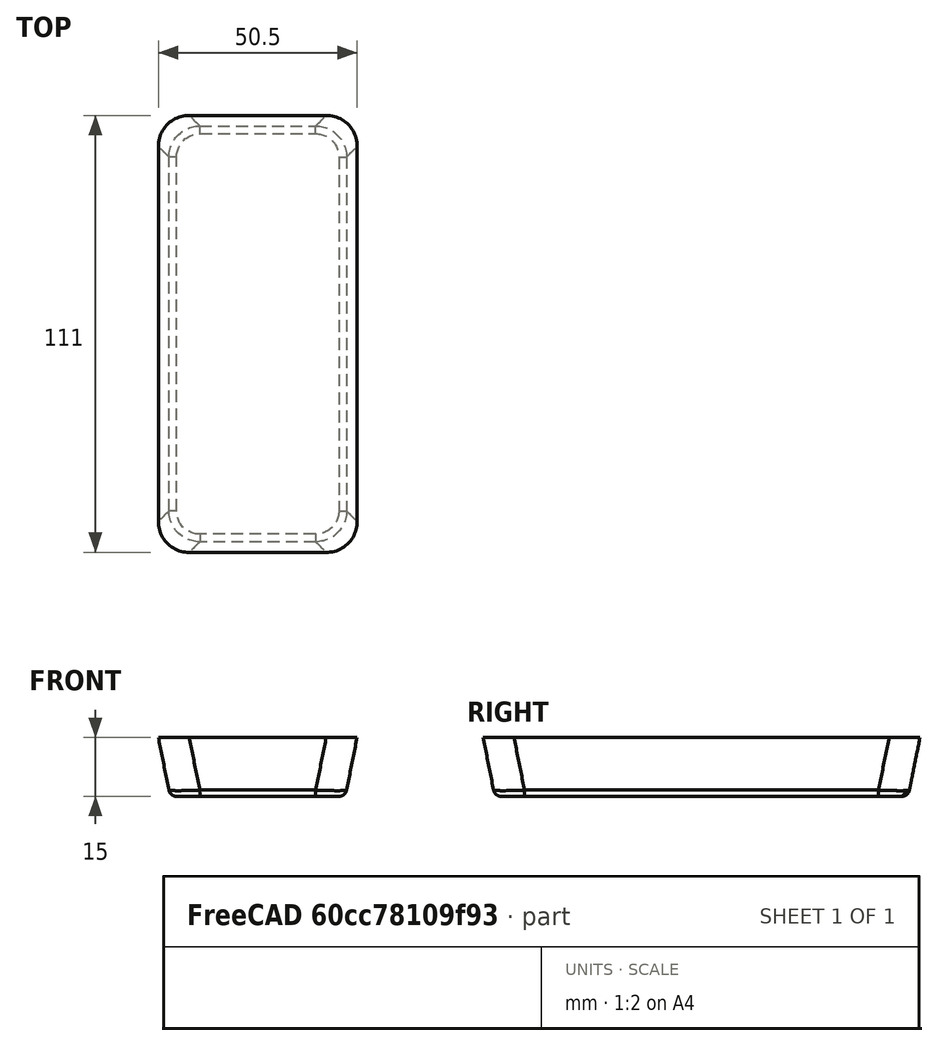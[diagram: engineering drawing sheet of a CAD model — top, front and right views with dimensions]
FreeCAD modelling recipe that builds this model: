
FCSTD DOCUMENT  (FreeCAD 0.20R29603 (Git))
Label: ParametricTray
License: All rights reserved
LicenseURL: http://en.wikipedia.org/wiki/All_rights_reserved
objects: TechDraw::DrawViewDimension×4, Sketcher::SketchObject×2, PartDesign::Fillet×2, TechDraw::DrawProjGroupItem×2, TechDraw::DrawViewBalloon×2, Spreadsheet::Sheet×1, PartDesign::AdditiveLoft×1, PartDesign::Body×1, TechDraw::DrawSVGTemplate×1, TechDraw::DrawProjGroup×1, TechDraw::DrawPage×1
note: 9 computed .brp shape members not serialized (recipe doc carries the construction recipe); baked Part::Feature solids carry a one-line shape summary decoded from their .brp

FEATURE [Spreadsheet::Sheet] Spreadsheet  label="data"
  cells = A1=Height; B1(height)==15mm; A2=Length; B2(length)==111mm; A3=Width; B3(width)==50.5mm; A4=Side Radius; B4(r_s)==8mm; A5=Bottom Radius; B5(r_b)==2mm; A6=Wall Gap; B6(gap)==3mm
FEATURE [Sketcher::SketchObject] Sketch  label="TopSketch"
  AttachmentOffset = pos=(0,0,15) rot=(0,0,1;0rad)
  FullyConstrained = true
  MapMode = 5
  Placement = pos=(0,0,15) rot=(0,0,1;0rad)
  Support = -> [XY_Plane]
  expr: .AttachmentOffset.Base.z = <<data>>.height
  expr: Constraints[10] = <<data>>.width
  expr: Constraints[9] = <<data>>.length
  sketch-geometry (4):
    g0: LineSegment StartX=0 StartY=0 StartZ=0 EndX=50.5 EndY=0 EndZ=0
    g1: LineSegment StartX=50.5 StartY=0 StartZ=0 EndX=50.5 EndY=111 EndZ=0
    g2: LineSegment StartX=50.5 StartY=111 StartZ=0 EndX=0 EndY=111 EndZ=0
    g3: LineSegment StartX=0 StartY=111 StartZ=0 EndX=0 EndY=0 EndZ=0
  constraints (11):
    c: Coincident(g0,g1)
    c: Coincident(g1,g2)
    c: Coincident(g2,g3)
    c: Coincident(g3,g0)
    c: Horizontal(g0)
    c: Horizontal(g2)
    c: Vertical(g1)
    c: Vertical(g3)
    c: Coincident(g0,g-1)
    c: DistanceY(g1,g1) = 111
    c: DistanceX(g0,g0) = 50.5
FEATURE [Sketcher::SketchObject] Sketch001  label="BottomSketch"
  ExternalGeometry = -> [Sketch]
  FullyConstrained = true
  MapMode = 5
  Support = -> [XY_Plane]
  expr: Constraints[10] = <<data>>.gap
  expr: Constraints[11] = <<data>>.gap
  expr: Constraints[8] = <<data>>.gap
  expr: Constraints[9] = <<data>>.gap
  sketch-geometry (4):
    g0: LineSegment StartX=3 StartY=108 StartZ=0 EndX=47.5 EndY=108 EndZ=0
    g1: LineSegment StartX=47.5 StartY=108 StartZ=0 EndX=47.5 EndY=3 EndZ=0
    g2: LineSegment StartX=47.5 StartY=3 StartZ=0 EndX=3 EndY=3 EndZ=0
    g3: LineSegment StartX=3 StartY=3 StartZ=0 EndX=3 EndY=108 EndZ=0
  constraints (12):
    c: Coincident(g0,g1)
    c: Coincident(g1,g2)
    c: Coincident(g2,g3)
    c: Coincident(g3,g0)
    c: Horizontal(g0)
    c: Horizontal(g2)
    c: Vertical(g1)
    c: Vertical(g3)
    c: DistanceX(g-3,g0) = 3
    c: DistanceY(g0,g-3) = 3
    c: DistanceY(g-4,g1) = 3
    c: DistanceX(g1,g-4) = 3
FEATURE [PartDesign::AdditiveLoft] AdditiveLoft
  Closed = false
  Profile = -> Sketch001
  Ruled = false
  Sections = -> [Sketch]
FEATURE [PartDesign::Fillet] Fillet
  Base = -> AdditiveLoft [Edge12,Edge11,Edge5,Edge7]
  BaseFeature = -> AdditiveLoft
  Radius = 8
  SupportTransform = false
  UseAllEdges = false
  expr: Radius = <<data>>.r_s
FEATURE [PartDesign::Fillet] Fillet001
  Base = -> Fillet [Face1]
  BaseFeature = -> Fillet
  Radius = 2
  SupportTransform = false
  UseAllEdges = false
  expr: Radius = <<data>>.r_b
FEATURE [PartDesign::Body] Body
  Group = -> [Sketch,Sketch001,AdditiveLoft,Fillet,Fillet001]
  Origin = -> Origin
  Tip = -> Fillet001
FEATURE [TechDraw::DrawSVGTemplate] Template
  EditableTexts = AUTHOR_NAME=<owner>; DN=DN; DRAWING_TITLE=Parametric Tray; FC-DATE=05/03/2023; FC-REV=REV A; FC-SC=SCALE; FC-SH=1 / 1; FC-SI=A4; FreeCAD_DRAWING=Parameters; PN=PN
  Height = 297
  Orientation = 0
  Width = 210
FEATURE [TechDraw::DrawProjGroupItem] ProjItem  label="Front"
  CoarseView = false
  Direction = (1,1e-16,0)
  Focus = 100
  HardHidden = false
  IsoCount = 0
  IsoHidden = false
  IsoVisible = false
  LockPosition = true
  Perspective = false
  Rotation = 0
  RotationVector = (-1,0,0)
  ScaleType = 2
  SeamHidden = false
  SeamVisible = true
  SmoothHidden = false
  SmoothVisible = true
  Source = -> [Body]
  Type = 0
  X = 0
  XDirection = (-1e-16,1,0)
  Y = 0
FEATURE [TechDraw::DrawViewBalloon] Balloon
  BubbleShape = 1
  EndType = 0
  EndTypeScale = 1
  KinkLength = 5
  LockPosition = false
  OriginX = 52.7607
  OriginY = -7.12815
  Rotation = 0
  ScaleType = 0
  ShapeScale = 1
  SourceView = -> ProjItem
  Text = Bottom Radius
  TextWrapLen = -1
  X = 41.1133
  Y = -20.7332
FEATURE [TechDraw::DrawViewDimension] Dimension002
  AngleOverride = false
  Arbitrary = true
  ArbitraryTolerances = false
  EqualTolerance = true
  ExtensionAngle = 0
  FormatSpec = Height
  FormatSpecOverTolerance = %+.2w
  FormatSpecUnderTolerance = %+.2w
  Inverted = false
  LineAngle = 0
  LockPosition = false
  MeasureType = 1
  OverTolerance = 0
  References2D = -> [ProjItem]
  Rotation = 0
  ScaleType = 0
  TheoreticalExact = false
  Type = 2
  UnderTolerance = 0
  X = 66.8677
  Y = 21.3376
FEATURE [TechDraw::DrawProjGroupItem] ProjItem003  label="Top"
  CoarseView = false
  Direction = (0,0,1)
  Focus = 100
  HardHidden = false
  IsoCount = 0
  IsoHidden = false
  IsoVisible = false
  LockPosition = false
  Perspective = false
  Rotation = 0
  RotationVector = (1,0,0)
  ScaleType = 2
  SeamHidden = false
  SeamVisible = true
  SmoothHidden = false
  SmoothVisible = true
  Source = -> [Body]
  Type = 4
  X = 0
  XDirection = (-1e-16,1,0)
  Y = -90.5
FEATURE [TechDraw::DrawProjGroup] ProjGroup
  Anchor = -> ProjItem
  AutoDistribute = true
  LockPosition = false
  ProjectionType = 0
  Rotation = 0
  ScaleType = 0
  Source = -> [Body]
  Views = -> [ProjItem,ProjItem003]
  X = 103.296
  Y = 240
  spacingX = 15
  spacingY = 40
FEATURE [TechDraw::DrawViewDimension] Dimension
  AngleOverride = false
  Arbitrary = true
  ArbitraryTolerances = false
  EqualTolerance = true
  ExtensionAngle = 0
  FormatSpec = Length
  FormatSpecOverTolerance = %+.2w
  FormatSpecUnderTolerance = %+.2w
  Inverted = false
  LineAngle = 0
  LockPosition = false
  MeasureType = 1
  OverTolerance = 0
  References2D = -> [ProjItem003]
  Rotation = 0
  ScaleType = 0
  TheoreticalExact = false
  Type = 1
  UnderTolerance = 0
  X = 0.33076
  Y = 43.8704
FEATURE [TechDraw::DrawViewDimension] Dimension003
  AngleOverride = false
  Arbitrary = true
  ArbitraryTolerances = false
  EqualTolerance = true
  ExtensionAngle = 0
  FormatSpec = Width
  FormatSpecOverTolerance = %+.2w
  FormatSpecUnderTolerance = %+.2w
  Inverted = false
  LineAngle = 0
  LockPosition = false
  MeasureType = 1
  OverTolerance = 0
  References2D = -> [ProjItem003]
  Rotation = 0
  ScaleType = 0
  TheoreticalExact = false
  Type = 2
  UnderTolerance = 0
  X = 67.6907
  Y = 6.2279
FEATURE [TechDraw::DrawViewBalloon] Balloon001
  BubbleShape = 1
  EndType = 0
  EndTypeScale = 1
  KinkLength = 5
  LockPosition = false
  OriginX = 53.5511
  OriginY = -22.9703
  Rotation = 0
  ScaleType = 0
  ShapeScale = 1
  SourceView = -> ProjItem003
  Text = Side Radius
  TextWrapLen = -1
  X = 41.5977
  Y = -38.1191
FEATURE [TechDraw::DrawViewDimension] Dimension004
  AngleOverride = false
  Arbitrary = true
  ArbitraryTolerances = false
  EqualTolerance = true
  ExtensionAngle = 0
  FormatSpec = Wall Gap
  FormatSpecOverTolerance = %+.2w
  FormatSpecUnderTolerance = %+.2w
  Inverted = false
  LineAngle = 0
  LockPosition = false
  MeasureType = 1
  OverTolerance = 0
  References2D = -> [ProjItem]
  Rotation = 0
  ScaleType = 0
  TheoreticalExact = false
  Type = 1
  UnderTolerance = 0
  X = -27.9512
  Y = -17.7187
FEATURE [TechDraw::DrawPage] Page
  KeepUpdated = true
  NextBalloonIndex = 5
  ProjectionType = 0
  Template = -> Template
  Views = -> [ProjGroup,Dimension002,Balloon,Dimension,Dimension003,Balloon001,Dimension004]
